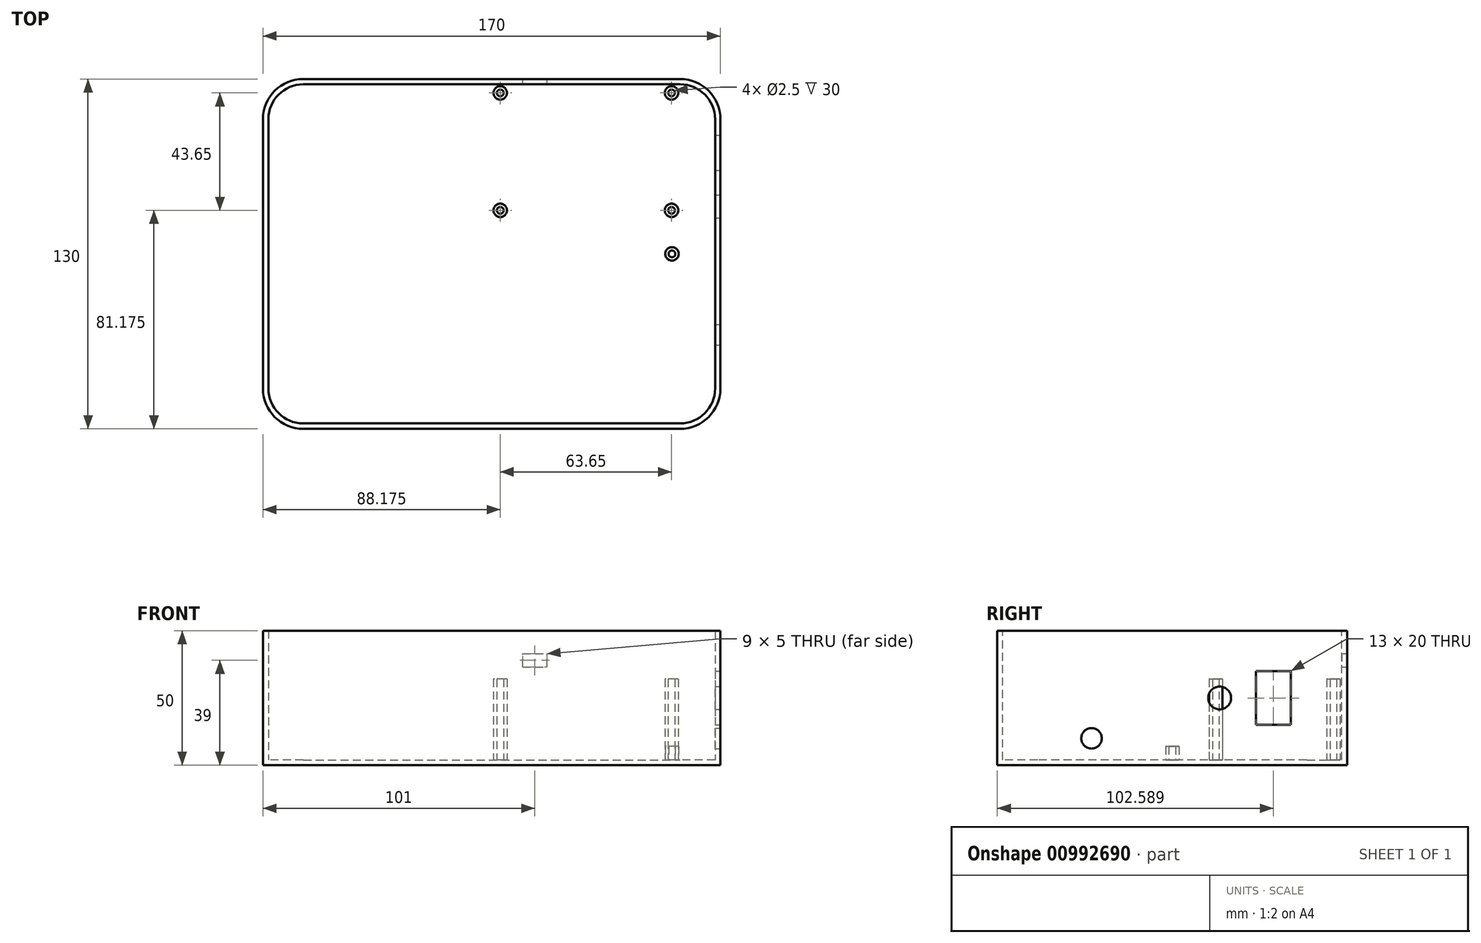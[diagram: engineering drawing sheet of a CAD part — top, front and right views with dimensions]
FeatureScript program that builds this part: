
annotation { "Feature Type Name" : "Feature", "Feature Type Description" : "" }
export const myFeature = defineFeature(function(context is Context, id is Id, definition is map)
    precondition{}
    {
        {
            var Q0;
            Q0=qCreatedBy(makeId("Top.planeOp"),FACE);
            var sketch = newSketch(context, id + "F0", { "sketchPlane" : qUnion([Q0])});
            skLineSegment(sketch, "E0.bottom", {"start": v(-70, 65) * mm, "end": v(70, 65) * mm});
            skLineSegment(sketch, "E0.top", {"start": v(-70, -65) * mm, "end": v(70, -65) * mm});
            skLineSegment(sketch, "E0.left", {"start": v(-85, 50) * mm, "end": v(-85, -50) * mm});
            skLineSegment(sketch, "E0.right", {"start": v(85, 50) * mm, "end": v(85, -50) * mm});
            skPoint(sketch, "E0.middle", {"position": v(0, 0) * mm});
            skPoint(sketch, "E1.visualSharp", {"position": v(-85, 65) * mm});
            skArc(sketch, "E1.filletArc", {"start": v(-70, 65) * mm, "mid": v(-80.6, 60.6) * mm, "end": v(-85, 50) * mm});
            skPoint(sketch, "E2.visualSharp", {"position": v(85, 65) * mm});
            skArc(sketch, "E2.filletArc", {"start": v(85, 50) * mm, "mid": v(80.6, 60.6) * mm, "end": v(70, 65) * mm});
            skPoint(sketch, "E3.visualSharp", {"position": v(85, -65) * mm});
            skArc(sketch, "E3.filletArc", {"start": v(70, -65) * mm, "mid": v(80.6, -60.6) * mm, "end": v(85, -50) * mm});
            skPoint(sketch, "E4.visualSharp", {"position": v(-85, -65) * mm});
            skArc(sketch, "E4.filletArc", {"start": v(-85, -50) * mm, "mid": v(-80.6, -60.6) * mm, "end": v(-70, -65) * mm});
            skSolve(sketch);
        }
        {
            var Q0;
            Q0=qSketchRegion(id+"F0",true);
            extrude(context, id + "F1", {"entities" : qUnion([Q0]), "depth" : 50 * mm, "offsetDistance" : 25 * mm});
        }
        {
            var Q0;
            Q0=makeQuery(id+"F1.opExtrude","CAP_FACE",FACE,{"disambiguationData":[OSD([sQuery(id+"F0.wireOp",EDGE,"E0.bottom"),sQuery(id+"F0.wireOp",EDGE,"E0.top"),sQuery(id+"F0.wireOp",EDGE,"E0.left"),sQuery(id+"F0.wireOp",EDGE,"E0.right"),sQuery(id+"F0.wireOp",EDGE,"E1.filletArc"),sQuery(id+"F0.wireOp",EDGE,"E2.filletArc"),sQuery(id+"F0.wireOp",EDGE,"E3.filletArc"),sQuery(id+"F0.wireOp",EDGE,"E4.filletArc")])],"isStart":false});
            shell(context, id + "F2", {"entities" : qUnion([Q0]), "thickness" : 2 * mm});
        }
        {
            var Q0;
            Q0=makeQuery(id+"F2.opShell","OFFSET_FACE",FACE,{"disambiguationData":[OSD([sQuery(id+"F0.wireOp",EDGE,"E0.bottom"),sQuery(id+"F0.wireOp",EDGE,"E0.top"),sQuery(id+"F0.wireOp",EDGE,"E0.left"),sQuery(id+"F0.wireOp",EDGE,"E0.right"),sQuery(id+"F0.wireOp",EDGE,"E1.filletArc"),sQuery(id+"F0.wireOp",EDGE,"E2.filletArc"),sQuery(id+"F0.wireOp",EDGE,"E3.filletArc"),sQuery(id+"F0.wireOp",EDGE,"E4.filletArc")])]});
            var sketch = newSketch(context, id + "F3", { "sketchPlane" : qUnion([Q0])});
            skCircle(sketch, "E5", {"center": v(3.18, 59.83) * mm, "radius": 2.5 * mm});
            skCircle(sketch, "E6.MirrorC", {"center": v(3.18, 16.17) * mm, "radius": 2.5 * mm});
            skCircle(sketch, "E7", {"center": v(66.83, 59.83) * mm, "radius": 2.5 * mm});
            skCircle(sketch, "E8.MirrorC", {"center": v(66.83, 16.17) * mm, "radius": 2.5 * mm});
            skCircle(sketch, "E9", {"center": v(3.18, 59.83) * mm, "radius": 1.25 * mm});
            skCircle(sketch, "E10", {"center": v(66.83, 59.83) * mm, "radius": 1.25 * mm});
            skCircle(sketch, "E11", {"center": v(66.83, 16.17) * mm, "radius": 1.25 * mm});
            skCircle(sketch, "E12", {"center": v(3.18, 16.17) * mm, "radius": 1.25 * mm});
            skSolve(sketch);
        }
        {
            var Q0;
            Q0=qSketchRegion(id+"F3",true);
            extrude(context, id + "F4", {"entities" : qUnion([Q0]), "operationType" : NewBodyOperationType.ADD, "depth" : 30 * mm, "offsetDistance" : 25 * mm});
        }
        {
            var Q0;
            Q0=makeQuery(id+"F1.opExtrude","SWEPT_FACE",FACE,{"disambiguationData":[OSD([sQuery(id+"F0.wireOp",EDGE,"E0.bottom")])]});
            var sketch = newSketch(context, id + "F5", { "sketchPlane" : qUnion([Q0])});
            skLineSegment(sketch, "E13.bottom", {"start": v(-11.5, 36.5) * mm, "end": v(-20.5, 36.5) * mm});
            skLineSegment(sketch, "E13.top", {"start": v(-11.5, 41.5) * mm, "end": v(-20.5, 41.5) * mm});
            skLineSegment(sketch, "E13.left", {"start": v(-11.5, 36.5) * mm, "end": v(-11.5, 41.5) * mm});
            skLineSegment(sketch, "E13.right", {"start": v(-20.5, 36.5) * mm, "end": v(-20.5, 41.5) * mm});
            skPoint(sketch, "E13.middle", {"position": v(-16, 39) * mm});
            skSolve(sketch);
        }
        {
            var Q0;
            Q0=qSketchRegion(id+"F5",true);
            extrude(context, id + "F6", {"entities" : qUnion([Q0]), "operationType" : NewBodyOperationType.REMOVE, "endBound" : BoundingType.UP_TO_NEXT, "oppositeDirection" : true, "depth" : 25 * mm, "offsetDistance" : 25 * mm});
        }
        {
            var Q0;
            Q0=makeQuery(id+"F1.opExtrude","CAP_FACE",FACE,{"disambiguationData":[OSD([sQuery(id+"F0.wireOp",EDGE,"E0.bottom"),sQuery(id+"F0.wireOp",EDGE,"E0.top"),sQuery(id+"F0.wireOp",EDGE,"E0.left"),sQuery(id+"F0.wireOp",EDGE,"E0.right"),sQuery(id+"F0.wireOp",EDGE,"E1.filletArc"),sQuery(id+"F0.wireOp",EDGE,"E2.filletArc"),sQuery(id+"F0.wireOp",EDGE,"E3.filletArc"),sQuery(id+"F0.wireOp",EDGE,"E4.filletArc")])],"isStart":false});
            var sketch = newSketch(context, id + "F7", { "sketchPlane" : qUnion([Q0])});
            skSolve(sketch);
        }
        {
            var Q0;
            Q0=makeQuery(id+"F1.opExtrude","SWEPT_FACE",FACE,{"disambiguationData":[OSD([sQuery(id+"F0.wireOp",EDGE,"E0.right")])]});
            var sketch = newSketch(context, id + "F8", { "sketchPlane" : qUnion([Q0])});
            skCircle(sketch, "E14", {"center": v(17.59, 25) * mm, "radius": 4.25 * mm});
            skLineSegment(sketch, "E15.bottom", {"start": v(44.09, 15) * mm, "end": v(31.09, 15) * mm});
            skLineSegment(sketch, "E15.top", {"start": v(44.09, 35) * mm, "end": v(31.09, 35) * mm});
            skLineSegment(sketch, "E15.left", {"start": v(44.09, 15) * mm, "end": v(44.09, 35) * mm});
            skLineSegment(sketch, "E15.right", {"start": v(31.09, 15) * mm, "end": v(31.09, 35) * mm});
            skPoint(sketch, "E15.middle", {"position": v(37.59, 25) * mm});
            skSolve(sketch);
        }
        {
            var Q0;
            Q0=qSketchRegion(id+"F8",true);
            extrude(context, id + "F9", {"entities" : qUnion([Q0]), "operationType" : NewBodyOperationType.REMOVE, "endBound" : BoundingType.UP_TO_NEXT, "oppositeDirection" : true, "depth" : 25 * mm, "offsetDistance" : 25 * mm});
        }
        {
            var Q0;
            {var subQ0=sQuery(id+"F0.wireOp",EDGE,"E0.right");var subQ1=sQuery(id+"F0.wireOp",EDGE,"E4.filletArc");var subQ2=sQuery(id+"F0.wireOp",EDGE,"E3.filletArc");var subQ3=sQuery(id+"F0.wireOp",EDGE,"E2.filletArc");var subQ4=sQuery(id+"F0.wireOp",EDGE,"E1.filletArc");var subQ5=sQuery(id+"F0.wireOp",EDGE,"E0.bottom");var subQ6=sQuery(id+"F0.wireOp",EDGE,"E0.top");var subQ7=sQuery(id+"F0.wireOp",EDGE,"E0.left");Q0=makeQuery(id+"F4.boolean.opBoolean","SPLIT",FACE,{"disambiguationData":[TD([makeQuery(id+"F2.opShell","OFFSET_FACE",FACE,{"disambiguationData":[OSD([subQ5])]})])],"derivedFrom":makeQuery(id+"F2.opShell","OFFSET_FACE",FACE,{"disambiguationData":[OSD([subQ5,subQ6,subQ7,subQ0,subQ4,subQ3,subQ2,subQ1])]})});}
            var sketch = newSketch(context, id + "F10", { "sketchPlane" : qUnion([Q0])});
            skCircle(sketch, "E16.0.3.2", {"center": v(66.97, 0) * mm, "radius": 2.5 * mm});
            skCircle(sketch, "E16.0.3.3", {"center": v(66.97, 0) * mm, "radius": 1.25 * mm});
            skLineSegment(sketch, "E17", {"start": v(3.18, 16.17) * mm, "end": v(66.83, 16.17) * mm, "construction": true});
            skSolve(sketch);
        }
        {
            var Q0;
            Q0=qSketchRegion(id+"F10",true);
            extrude(context, id + "F11", {"entities" : qUnion([Q0]), "operationType" : NewBodyOperationType.ADD, "depth" : 5 * mm, "offsetDistance" : 25 * mm});
        }
        {
            var Q0;
            Q0=makeQuery(id+"F1.opExtrude","SWEPT_FACE",FACE,{"disambiguationData":[OSD([sQuery(id+"F0.wireOp",EDGE,"E0.right")])]});
            var sketch = newSketch(context, id + "F12", { "sketchPlane" : qUnion([Q0])});
            skCircle(sketch, "E18", {"center": v(-30, 10) * mm, "radius": 3.81 * mm});
            skSolve(sketch);
        }
        {
            var Q0;
            Q0 = qSketchRegion(id + "F12", true);
            extrude(context, id + "F13", {"entities" : qUnion([Q0]), "operationType" : NewBodyOperationType.REMOVE, "oppositeDirection" : true, "depth" : 25 * mm, "offsetDistance" : 25 * mm});
        }
    });
